# Revit family: Incepa_Waterpress_Válvula para Mictório de Parede_B5002I8CRB
name_source: partatom
category: Plumbing Fixtures
revit_build: Autodesk Revit Architecture 2014 (Build: 20131024_2115(x64)
units: mm (PartAtom-declared; Revit-internal decimal feet)

## types (1)
- Torneira de parede
    Assembly Code = D2010
    CW Connection = No
    CWFU = 1
    Cost = 0 $
    Default Elevation = 0 mm  [stored 0 ft]
    Description = Válvula mictório de parede com fechamento automático (B5002I8CRB), linha Eco Press - Metais Incepa
    Desenvolvido por = ofcdesk
    HW Connection = No
    HWFU = 0
    Incepa: Categoria = Lavatório
    Incepa: Cores Disponíveis = Cromado
    Incepa: Código = B5002I8CRB
    Incepa: Descrição = Válvula mictório de parede com fechamento automático (B5002I8CRB), linha Eco Press - Metais Incepa
    Incepa: Fabricante = Incepa
    Incepa: Linha = Eco Press
    Incepa: Produto = Metais
    Incepa: Tipo = Válvulas
    Incepa: Versão = Autodesk Revit MEP 2014
    Manufacturer = Incepa
    Model = B5002I8CRB
    Selo de Qualidade ofcdesk = Standard
    URL = http://www.incepa.com.br
    Vent Connection = No
    WFU = 0
    Waste Connection = No

note: [stored X ft] marks values corroborated as IEEE doubles in the binary element streams (Revit-internal decimal feet)

## geometry (parser evidence)
native form markers: Blend x2, Sweep x1
no freeform markers — native parametric forms only
